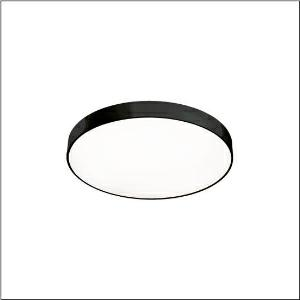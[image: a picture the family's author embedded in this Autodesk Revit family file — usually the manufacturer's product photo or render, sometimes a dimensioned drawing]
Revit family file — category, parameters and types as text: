
# Revit family: round_21_m_51mr36gd0321b
name_source: partatom
category: Lighting Fixtures
units: mm (PartAtom-declared; Revit-internal decimal feet)

## family parameters
Cut with Voids When Loaded = No
Host = Face
Light Source = No
Part Type = Normal
Room Calculation Point = No
Round Connector Dimension = Use Diameter
Shared = No

## types (1)
- Round 21 M (1 x LED, 6840 lm, 54.5 W, 3000K)
    Apparent Load = 55 VA
    CIE Flux Codes = 49 80 96 85 100
    Color Rendering = 80
    Color Temperature = 3000K
    Default Elevation = 1800 mm
    Description = Round 21 M, wall and ceiling luminaire, primary optical cover: cover, of PMMA, opal, light emission: direct/indirect distribution, primary light characteristic: symmetric, installation type: suspended mounting, surface-mounted, LED, rated luminous flux: 6.790lm, luminous efficacy: 124lm/W, light colour: 830, colour temperature: 3000K, with terminal, 5-pole, mains connection: 230V, AC, 50/60Hz, rated input power: 55W, housing, of aluminium, coated, black, diameter: 600mm, height: 62mm, protection rating (complete): IP40, insulation class (complete): insulation class I (protective earthing), certification: CE, impact resistance: IK04, permissible operating ambient temperature: -10..+35°C, packaging unit: 1 piece
    Height = 87 mm
    Lamp = 1 x LED
    Lamp Light Flux = 6840 lm
    Lamp Power = 54.5 W
    Lamp count = 1
    Length = 600 mm
    Luminous efficacy = 126 lm/W
    Manufacturer = Siteco
    ModVariant = No
    Model = 51MR36GD0321B
    Mounting Place = Ceiling
    Mounting Type = Surface mounted
    Number of Poles = 1
    OnlyDefault = Yes
    Power Factor = 1
    Product Name = Round 21 M
    Product group = wall and ceiling luminaire
    ProductGroupID = 301
    Protection Class = Protection class I
    Protection Degree = IP 40
    RLX_Detail_Level = 1
    RLX_Emergency_Light_Flux = 0 lm
    RLX_Emergency_Type = 0
    RLX_Emergency_Type_DB = No
    RlxData = <blob elided: 18101 chars, md5=38bd8694>
    Socket = socket
    Standby Power = 0 W
    System Light Flux = 6840 lm
    System Power = 55 W
    Type Comments = Product without accessories
    Type Image = l_1258332.jpg
    URL = http://relux.com
    VarID = ---
    Voltage = 0 V
    Weight = 0.00 kg
    Width = 0 mm  [stored 0 ft]

note: [stored X ft] marks values corroborated as IEEE doubles in the binary element streams (Revit-internal decimal feet)

## geometry (parser evidence)
native form markers: Blend x4, Sweep x15
no freeform markers — native parametric forms only
